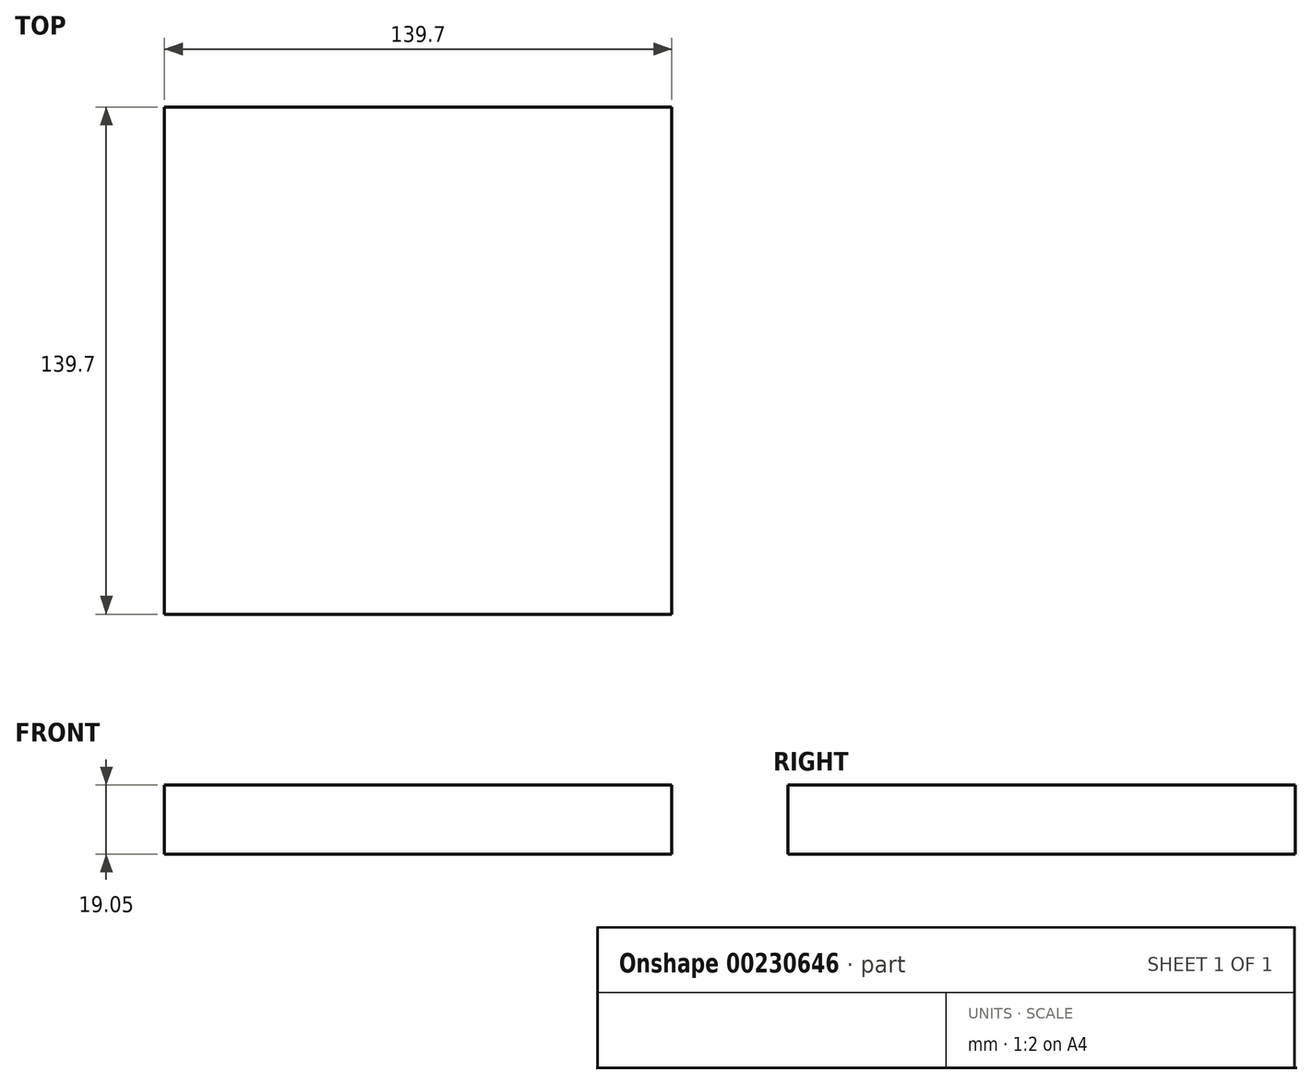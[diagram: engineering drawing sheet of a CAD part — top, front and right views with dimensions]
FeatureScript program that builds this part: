
annotation { "Feature Type Name" : "Feature", "Feature Type Description" : "" }
export const myFeature = defineFeature(function(context is Context, id is Id, definition is map)
    precondition{}
    {
        {
            var Q0;
            Q0=qCreatedBy(makeId("Top.planeOp"),FACE);
            var sketch = newSketch(context, id + "F0", { "sketchPlane" : qUnion([Q0])});
            skLineSegment(sketch, "E0.bottom", {"start": v(69.85, 69.85) * mm, "end": v(-69.85, 69.85) * mm});
            skLineSegment(sketch, "E0.top", {"start": v(69.85, -69.85) * mm, "end": v(-69.85, -69.85) * mm});
            skLineSegment(sketch, "E0.left", {"start": v(69.85, 69.85) * mm, "end": v(69.85, -69.85) * mm});
            skLineSegment(sketch, "E0.right", {"start": v(-69.85, 69.85) * mm, "end": v(-69.85, -69.85) * mm});
            skPoint(sketch, "E0.middle", {"position": v(0, 0) * mm});
            skSolve(sketch);
        }
        {
            var Q0;
            Q0=makeQuery(id+"F0.imprint","IMPRINT",FACE,{"disambiguationData":[TD([[makeQuery(id+"F0.imprint","IMPRINT",EDGE,{"derivedFrom":sQuery(id+"F0.wireOp",EDGE,"E0.bottom")}),1.0]])]});
            extrude(context, id + "F1", {"entities" : qUnion([Q0]), "depth" : 19.05 * mm});
        }
    });
